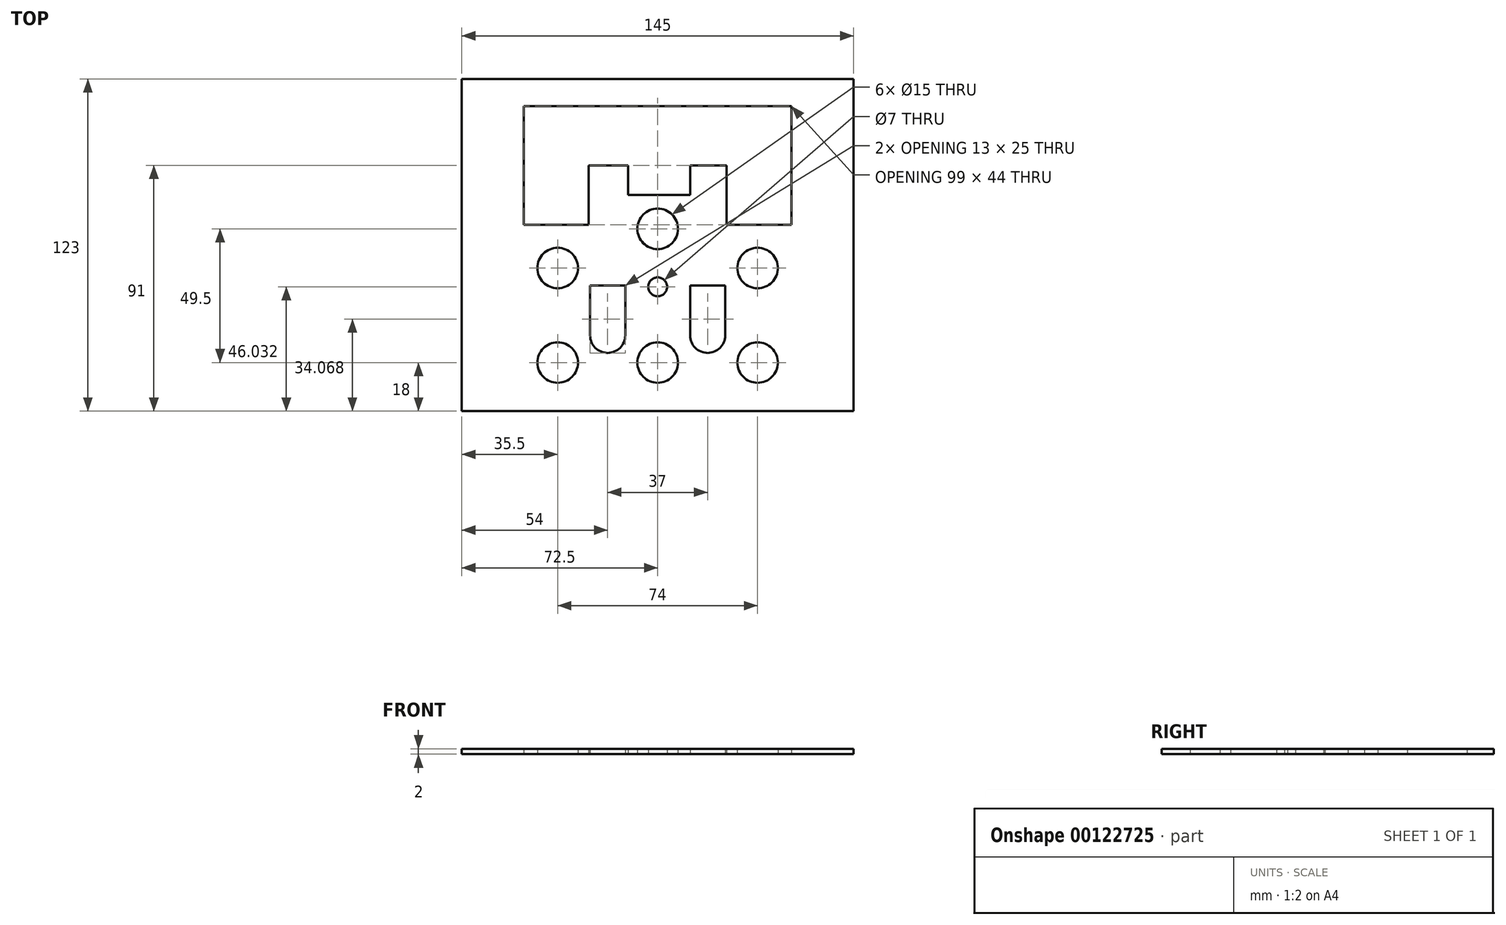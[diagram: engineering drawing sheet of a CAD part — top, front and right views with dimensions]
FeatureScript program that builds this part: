
annotation { "Feature Type Name" : "Feature", "Feature Type Description" : "" }
export const myFeature = defineFeature(function(context is Context, id is Id, definition is map)
    precondition{}
    {
        {
            var Q0;
            Q0=qCreatedBy(makeId("Top.planeOp"),FACE);
            var sketch = newSketch(context, id + "F0", { "sketchPlane" : qUnion([Q0])});
            skLineSegment(sketch, "E0.bottom", {"start": v(0, 0) * mm, "end": v(145, 0) * mm});
            skLineSegment(sketch, "E0.left", {"start": v(0, 0) * mm, "end": v(0, -123) * mm});
            skLineSegment(sketch, "E0.right", {"start": v(145, 0) * mm, "end": v(145, -123) * mm});
            skLineSegment(sketch, "E1", {"start": v(0, -123) * mm, "end": v(145, -123) * mm});
            skLineSegment(sketch, "E2", {"start": v(23, -10) * mm, "end": v(23, -54) * mm});
            skLineSegment(sketch, "E3", {"start": v(23, -54) * mm, "end": v(47, -54) * mm});
            skLineSegment(sketch, "E4", {"start": v(47, -54) * mm, "end": v(47, -32) * mm});
            skLineSegment(sketch, "E5", {"start": v(47, -32) * mm, "end": v(98, -32) * mm});
            skLineSegment(sketch, "E6", {"start": v(98, -32) * mm, "end": v(98, -54) * mm});
            skLineSegment(sketch, "E7", {"start": v(122, -54) * mm, "end": v(122, -10) * mm});
            skLineSegment(sketch, "E8", {"start": v(122, -10) * mm, "end": v(23, -10) * mm});
            skLineSegment(sketch, "E9", {"start": v(98, -54) * mm, "end": v(122, -54) * mm});
            skLineSegment(sketch, "E10.bottom", {"start": v(49, -10) * mm, "end": v(71, -10) * mm, "construction": true});
            skLineSegment(sketch, "E10.top", {"start": v(49, -20) * mm, "end": v(71, -20) * mm, "construction": true});
            skLineSegment(sketch, "E10.left", {"start": v(49, -10) * mm, "end": v(49, -20) * mm, "construction": true});
            skLineSegment(sketch, "E10.right", {"start": v(71, -10) * mm, "end": v(71, -20) * mm, "construction": true});
            skLineSegment(sketch, "E11.bottom", {"start": v(74, -10) * mm, "end": v(96, -10) * mm, "construction": true});
            skLineSegment(sketch, "E11.top", {"start": v(74, -20) * mm, "end": v(96, -20) * mm, "construction": true});
            skLineSegment(sketch, "E11.left", {"start": v(74, -10) * mm, "end": v(74, -20) * mm, "construction": true});
            skLineSegment(sketch, "E11.right", {"start": v(96, -10) * mm, "end": v(96, -20) * mm, "construction": true});
            skLineSegment(sketch, "E12.bottom", {"start": v(99, -10) * mm, "end": v(121, -10) * mm, "construction": true});
            skLineSegment(sketch, "E12.top", {"start": v(99, -20) * mm, "end": v(121, -20) * mm, "construction": true});
            skLineSegment(sketch, "E12.left", {"start": v(99, -10) * mm, "end": v(99, -20) * mm, "construction": true});
            skLineSegment(sketch, "E12.right", {"start": v(121, -10) * mm, "end": v(121, -20) * mm, "construction": true});
            skCircle(sketch, "E13", {"center": v(72.5, -55.5) * mm, "radius": 7.5 * mm});
            skCircle(sketch, "E14", {"center": v(35.5, -70) * mm, "radius": 7.5 * mm});
            skLineSegment(sketch, "E15.bottom", {"start": v(61.5, -32) * mm, "end": v(84.5, -32) * mm});
            skLineSegment(sketch, "E15.top", {"start": v(61.5, -43) * mm, "end": v(84.5, -43) * mm});
            skLineSegment(sketch, "E15.left", {"start": v(61.5, -32) * mm, "end": v(61.5, -43) * mm});
            skLineSegment(sketch, "E15.right", {"start": v(84.5, -32) * mm, "end": v(84.5, -43) * mm});
            skLineSegment(sketch, "E16.bottom", {"start": v(24, -10) * mm, "end": v(46, -10) * mm, "construction": true});
            skLineSegment(sketch, "E16.top", {"start": v(24, -20) * mm, "end": v(46, -20) * mm, "construction": true});
            skLineSegment(sketch, "E16.left", {"start": v(24, -10) * mm, "end": v(24, -20) * mm});
            skLineSegment(sketch, "E16.right", {"start": v(46, -10) * mm, "end": v(46, -20) * mm, "construction": true});
            skCircle(sketch, "E17", {"center": v(109.5, -105) * mm, "radius": 7.5 * mm});
            skCircle(sketch, "E18", {"center": v(109.5, -70) * mm, "radius": 7.5 * mm});
            skCircle(sketch, "E19", {"center": v(35.5, -105) * mm, "radius": 7.5 * mm});
            skLineSegment(sketch, "E20.bottom", {"start": v(24, -21) * mm, "end": v(46, -21) * mm, "construction": true});
            skLineSegment(sketch, "E20.top", {"start": v(24, -31) * mm, "end": v(46, -31) * mm, "construction": true});
            skLineSegment(sketch, "E20.left", {"start": v(24, -21) * mm, "end": v(24, -31) * mm, "construction": true});
            skLineSegment(sketch, "E20.right", {"start": v(46, -21) * mm, "end": v(46, -31) * mm, "construction": true});
            skLineSegment(sketch, "E21.bottom", {"start": v(24, -32) * mm, "end": v(46, -32) * mm, "construction": true});
            skLineSegment(sketch, "E21.top", {"start": v(24, -42) * mm, "end": v(46, -42) * mm, "construction": true});
            skLineSegment(sketch, "E21.left", {"start": v(24, -32) * mm, "end": v(24, -42) * mm, "construction": true});
            skLineSegment(sketch, "E21.right", {"start": v(46, -32) * mm, "end": v(46, -42) * mm, "construction": true});
            skLineSegment(sketch, "E22.bottom", {"start": v(24, -43) * mm, "end": v(46, -43) * mm, "construction": true});
            skLineSegment(sketch, "E22.top", {"start": v(24, -53) * mm, "end": v(46, -53) * mm, "construction": true});
            skLineSegment(sketch, "E22.left", {"start": v(24, -43) * mm, "end": v(24, -53) * mm, "construction": true});
            skLineSegment(sketch, "E22.right", {"start": v(46, -43) * mm, "end": v(46, -53) * mm, "construction": true});
            skPoint(sketch, "E23", {"position": v(47, -43) * mm});
            skCircle(sketch, "E24", {"center": v(72.5, -105) * mm, "radius": 7.5 * mm});
            skCircle(sketch, "E25", {"center": v(72.5, -76.97) * mm, "radius": 6.5 * mm, "construction": true});
            skCircle(sketch, "E26", {"center": v(72.5, -76.97) * mm, "radius": 3.5 * mm});
            skLineSegment(sketch, "E27.bottom", {"start": v(47.5, -76.43) * mm, "end": v(60.5, -76.43) * mm});
            skLineSegment(sketch, "E27.top", {"start": v(54, -101.43) * mm, "end": v(54, -101.43) * mm});
            skLineSegment(sketch, "E27.left", {"start": v(47.5, -76.43) * mm, "end": v(47.5, -94.93) * mm});
            skLineSegment(sketch, "E27.right", {"start": v(60.5, -76.43) * mm, "end": v(60.5, -94.93) * mm});
            skPoint(sketch, "E28.visualSharp", {"position": v(47.5, -101.43) * mm});
            skArc(sketch, "E28.filletArc", {"start": v(47.5, -94.93) * mm, "mid": v(49.4, -99.53) * mm, "end": v(54, -101.43) * mm});
            skPoint(sketch, "E29.visualSharp", {"position": v(60.5, -101.43) * mm});
            skArc(sketch, "E29.filletArc", {"start": v(54, -101.43) * mm, "mid": v(58.6, -99.53) * mm, "end": v(60.5, -94.93) * mm});
            skLineSegment(sketch, "E30.bottom", {"start": v(84.5, -76.43) * mm, "end": v(97.5, -76.43) * mm});
            skLineSegment(sketch, "E30.top", {"start": v(91, -101.43) * mm, "end": v(91, -101.43) * mm});
            skLineSegment(sketch, "E30.left", {"start": v(84.5, -76.43) * mm, "end": v(84.5, -94.93) * mm});
            skLineSegment(sketch, "E30.right", {"start": v(97.5, -76.43) * mm, "end": v(97.5, -94.93) * mm});
            skPoint(sketch, "E31.visualSharp", {"position": v(84.5, -101.43) * mm});
            skArc(sketch, "E31.filletArc", {"start": v(84.5, -94.93) * mm, "mid": v(86.4, -99.53) * mm, "end": v(91, -101.43) * mm});
            skPoint(sketch, "E32.visualSharp", {"position": v(97.5, -101.43) * mm});
            skArc(sketch, "E32.filletArc", {"start": v(91, -101.43) * mm, "mid": v(95.6, -99.53) * mm, "end": v(97.5, -94.93) * mm});
            skLineSegment(sketch, "E33.bottom", {"start": v(49, -21) * mm, "end": v(71, -21) * mm, "construction": true});
            skLineSegment(sketch, "E33.top", {"start": v(49, -31) * mm, "end": v(71, -31) * mm, "construction": true});
            skLineSegment(sketch, "E33.left", {"start": v(49, -21) * mm, "end": v(49, -31) * mm, "construction": true});
            skLineSegment(sketch, "E33.right", {"start": v(71, -21) * mm, "end": v(71, -31) * mm, "construction": true});
            skLineSegment(sketch, "E34.bottom", {"start": v(74, -21) * mm, "end": v(96, -21) * mm, "construction": true});
            skLineSegment(sketch, "E34.top", {"start": v(74, -31) * mm, "end": v(96, -31) * mm, "construction": true});
            skLineSegment(sketch, "E34.left", {"start": v(74, -21) * mm, "end": v(74, -31) * mm, "construction": true});
            skLineSegment(sketch, "E34.right", {"start": v(96, -21) * mm, "end": v(96, -31) * mm, "construction": true});
            skLineSegment(sketch, "E35.bottom", {"start": v(99, -21) * mm, "end": v(121, -21) * mm, "construction": true});
            skLineSegment(sketch, "E35.top", {"start": v(99, -31) * mm, "end": v(121, -31) * mm, "construction": true});
            skLineSegment(sketch, "E35.left", {"start": v(99, -21) * mm, "end": v(99, -31) * mm, "construction": true});
            skLineSegment(sketch, "E35.right", {"start": v(121, -21) * mm, "end": v(121, -31) * mm, "construction": true});
            skLineSegment(sketch, "E36.bottom", {"start": v(99, -32) * mm, "end": v(121, -32) * mm, "construction": true});
            skLineSegment(sketch, "E36.top", {"start": v(99, -42) * mm, "end": v(121, -42) * mm, "construction": true});
            skLineSegment(sketch, "E36.left", {"start": v(99, -32) * mm, "end": v(99, -42) * mm, "construction": true});
            skLineSegment(sketch, "E36.right", {"start": v(121, -32) * mm, "end": v(121, -42) * mm, "construction": true});
            skSolve(sketch);
        }
        {
            var Q0;
            Q0=qSketchRegion(id+"F0",true);
            extrude(context, id + "F1", {"entities" : qUnion([Q0]), "depth" : 2 * mm});
        }
    });
